# Revit family: ME-304
name_source: partatom
category: Aparatos sanitarios
units: mm (PartAtom-declared; Revit-internal decimal feet)

## family parameters
Compartido = Sí
Corte con vacíos al cargar = No
Cota de conector redondo = Diámetro de uso
Número OmniClass = 23.45.55.17
Punto de cálculo de habitación = Sí
Se basa en plano de trabajo = Sí
Siempre vertical = Sí
Tipo de pieza = Normal
Título OmniClass = Mixing Faucets

## types (1)
- MEP-2115
    Brass Chromed = Brass
    Comentarios de tipo = Mezcladora de 8" a 12"
    Descripción = Ensamble de 8" a 12" con desagüe de push.
    Elevación por defecto = 1"
    Fabricante = HELVEX S.A. de C.V.
    Features = Incluye herramienta de sujeción, contra de desagüe automático con rebosadero y aireador.
    Imagen de tipo = ME-304.jpg
    Inlet Threads = ½" - 14 NPSM
    Installation Adjustment = Instalación a  8", 10" y 12"
    Max. Working Pressure = 85.3 psi
    Min. Working Pressure = 14.2 psi
    Modelo = ME-304
    Support Base Diameter = 2"
    Total Height = 15"
    Total Length = 10"
    Total Width = 13"
    URL = https://www.helvex.com.mx

## geometry (parser evidence)
native form markers: Sweep x3
no freeform markers — native parametric forms only
